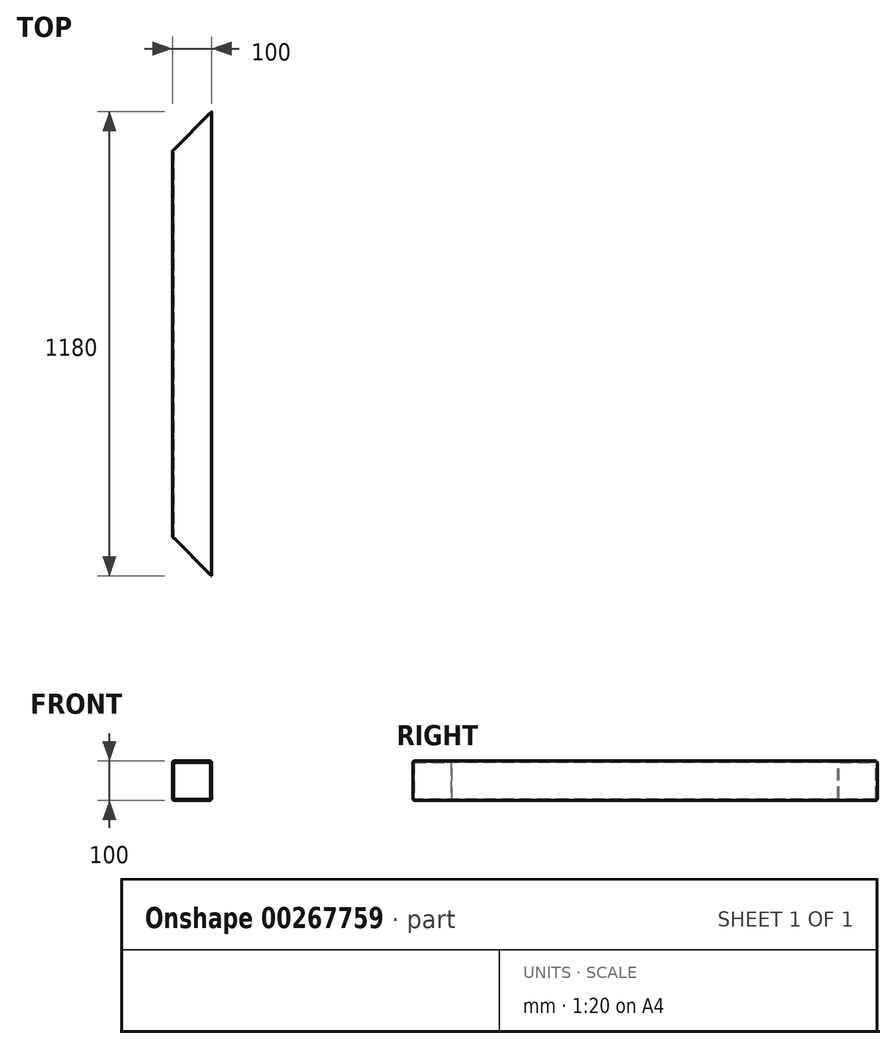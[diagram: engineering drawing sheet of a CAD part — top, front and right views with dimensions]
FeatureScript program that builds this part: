
annotation { "Feature Type Name" : "Feature", "Feature Type Description" : "" }
export const myFeature = defineFeature(function(context is Context, id is Id, definition is map)
    precondition{}
    {
        {
            var Q0;
            Q0=qCreatedBy(makeId("Front.planeOp"),FACE);
            var sketch = newSketch(context, id + "F0", { "sketchPlane" : qUnion([Q0])});
            skLineSegment(sketch, "E0.bottom", {"start": v(45, 50) * mm, "end": v(-45, 50) * mm});
            skLineSegment(sketch, "E0.top", {"start": v(45, -50) * mm, "end": v(-45, -50) * mm});
            skLineSegment(sketch, "E0.left", {"start": v(50, 45) * mm, "end": v(50, -45) * mm});
            skLineSegment(sketch, "E0.right", {"start": v(-50, 45) * mm, "end": v(-50, -45) * mm});
            skPoint(sketch, "E0.middle", {"position": v(0, 0) * mm});
            skPoint(sketch, "E1.visualSharp", {"position": v(-50, 50) * mm});
            skArc(sketch, "E1.filletArc", {"start": v(-45, 50) * mm, "mid": v(-48.54, 48.54) * mm, "end": v(-50, 45) * mm});
            skPoint(sketch, "E2.visualSharp", {"position": v(50, 50) * mm});
            skArc(sketch, "E2.filletArc", {"start": v(50, 45) * mm, "mid": v(48.54, 48.54) * mm, "end": v(45, 50) * mm});
            skPoint(sketch, "E3.visualSharp", {"position": v(50, -50) * mm});
            skArc(sketch, "E3.filletArc", {"start": v(45, -50) * mm, "mid": v(48.54, -48.54) * mm, "end": v(50, -45) * mm});
            skPoint(sketch, "E4.visualSharp", {"position": v(-50, -50) * mm});
            skArc(sketch, "E4.filletArc", {"start": v(-50, -45) * mm, "mid": v(-48.54, -48.54) * mm, "end": v(-45, -50) * mm});
            skArc(sketch, "E5.0", {"start": v(-45, 47) * mm, "mid": v(-46.41, 46.41) * mm, "end": v(-47, 45) * mm});
            skLineSegment(sketch, "E5.1", {"start": v(45, 47) * mm, "end": v(-45, 47) * mm});
            skLineSegment(sketch, "E5.2", {"start": v(-47, 45) * mm, "end": v(-47, -45) * mm});
            skArc(sketch, "E5.3", {"start": v(47, 45) * mm, "mid": v(46.41, 46.41) * mm, "end": v(45, 47) * mm});
            skArc(sketch, "E5.4", {"start": v(-47, -45) * mm, "mid": v(-46.41, -46.41) * mm, "end": v(-45, -47) * mm});
            skLineSegment(sketch, "E5.5", {"start": v(45, -47) * mm, "end": v(-45, -47) * mm});
            skArc(sketch, "E5.6", {"start": v(45, -47) * mm, "mid": v(46.41, -46.41) * mm, "end": v(47, -45) * mm});
            skLineSegment(sketch, "E5.7", {"start": v(47, 45) * mm, "end": v(47, -45) * mm});
            skSolve(sketch);
        }
        {
            var Q0;
            Q0=makeQuery(id+"F0.imprint","IMPRINT",FACE,{"disambiguationData":[TD([[makeQuery(id+"F0.imprint","IMPRINT",EDGE,{"derivedFrom":sQuery(id+"F0.wireOp",EDGE,"E0.bottom")}),1.0]])]});
            extrude(context, id + "F1", {"entities" : qUnion([Q0]), "oppositeDirection" : true, "depth" : 1180 * mm});
        }
        {
            var Q0;
            Q0=makeQuery(id+"F1.opExtrude","SWEPT_FACE",FACE,{"disambiguationData":[OSD([sQuery(id+"F0.wireOp",EDGE,"E0.bottom")])]});
            cPlane(context, id + "F2", {"entities" : qUnion([Q0]), "cplaneType" : CPlaneType.OFFSET, "offset" : 0 * mm, "width" : 150 * mm, "height" : 150 * mm});
        }
        {
            var Q0;
            Q0=qCreatedBy(id+"F2.planeOp",FACE);
            var sketch = newSketch(context, id + "F3", { "sketchPlane" : qUnion([Q0])});
            skLineSegment(sketch, "E6.bottom", {"start": v(-50, 0) * mm, "end": v(50, 0) * mm});
            skLineSegment(sketch, "E6.top", {"start": v(-50, 100) * mm, "end": v(50, 100) * mm, "construction": true});
            skLineSegment(sketch, "E6.left", {"start": v(-50, 0) * mm, "end": v(-50, 100) * mm});
            skLineSegment(sketch, "E6.right", {"start": v(50, 0) * mm, "end": v(50, 100) * mm, "construction": true});
            skLineSegment(sketch, "E7", {"start": v(50, 0) * mm, "end": v(-50, 100) * mm});
            skLineSegment(sketch, "E8.bottom", {"start": v(-50, 1180) * mm, "end": v(50, 1180) * mm});
            skLineSegment(sketch, "E8.top", {"start": v(-50, 1080) * mm, "end": v(50, 1080) * mm, "construction": true});
            skLineSegment(sketch, "E8.left", {"start": v(-50, 1180) * mm, "end": v(-50, 1080) * mm});
            skLineSegment(sketch, "E8.right", {"start": v(50, 1180) * mm, "end": v(50, 1080) * mm, "construction": true});
            skLineSegment(sketch, "E9", {"start": v(-50, 1080) * mm, "end": v(50, 1180) * mm});
            skSolve(sketch);
        }
        {
            var Q0;
            Q0=makeQuery(id+"F3.imprint","IMPRINT",FACE,{"disambiguationData":[TD([[makeQuery(id+"F3.imprint","IMPRINT",EDGE,{"derivedFrom":sQuery(id+"F3.wireOp",EDGE,"E6.bottom")}),1.0]])]});
            extrude(context, id + "F4", {"entities" : qUnion([Q0]), "operationType" : NewBodyOperationType.REMOVE, "endBound" : BoundingType.THROUGH_ALL, "oppositeDirection" : true, "depth" : 25 * mm});
        }
        {
            var Q0;
            Q0=qSketchRegion(id+"F3",true);
            extrude(context, id + "F5", {"entities" : qUnion([Q0]), "operationType" : NewBodyOperationType.REMOVE, "endBound" : BoundingType.THROUGH_ALL, "oppositeDirection" : true, "depth" : 25 * mm});
        }
    });
